# Revit family: equip-sink-elkay-scrub-wall-esswc
name_source: partatom
category: Plumbing Fixtures
units: mm (PartAtom-declared; Revit-internal decimal feet)

## family parameters
Cut with Voids When Loaded = No
Host = Face
Part Type = Normal
Room Calculation Point = No
Round Connector Dimension = Use Radius
Shared = No

## types (3) — shared parameters
AC Power = No
Assembly Code = D2010410
Backsplash Height = 1' - 0"
Backsplash Width = 0' - 2"
Backsplash Width Hidden = 0' - 2"
Bowl Depth = 1' - 0"
Bubbler CW Flow Rate = 2 GPM
Bubbler Material = Metal - Steel - Stainless - Chrome
Bubbler Nominal Dia = 0' - 0 1/2"
Bubbler Nominal Radius = 0' - 0 1/4"
CW Flow Rate = 2 GPM
Cost = 1 $
Default Elevation = 2' - 4 9/32"
Description = Wash-Up Lavatory Sinks
Distance Between Rough-In Water Supplies = 0' - 8"
Drain Material = Metal - Steel - Stainless - Chrome
Drain Part = LK173
Faucet CL from Top Backsplash = 0' - 3"
Faucet Hole Dia = 0' - 1 1/2"
Faucet Hole One = No
Faucet Hole One Top = 0' - 0 1/8"
Faucet Hole One to CL = 0' - 4"
Faucet Hole Two = No
Faucet Hole Two Top = 0' - 0 1/8"
Faucet Material = Metal - Steel - Stainless - Chrome
Faucet Part = LK940-BP07-L2
Faucet Water Supply Radius = 0' - 0 3/16"
HW Flow Rate = 2 GPM
Hole One to Two = 0' - 8"
Hole Radius = 0' - 0 3/4"
Keynote = D2010410
Manufacturer = Elkay Manufacturing
MasterFormat Number = 22.42.16.16
MasterFormat Title = Commercial Sinks
Mechanical Mix Valve = No
No Mix Valve = No
Nominal Dia = 0' - 0 1/2"
Nominal Radius = 0' - 0 1/4"
OmniClass Code = 23.45.05.14.14.27
OmniClass Title = Service Sinks
Plan View 2D = No
Reference Level to Back Plane = 0' - 0"
Rough-In Sanitary Installation Height = 0' - 11"
Rough-In Sanitary Right From CL Sink = 0' - 0"
Rough-In Water Supply Distance Left from CL Sink = 0' - 4"
Rough-In Water Supply Installation Height = 3' - 7 9/32"
Sanitary Flow Rate = 10 GPM
Sanitary Nominal Dia = 0' - 3"
Sanitary Nominal Radius = 0' - 1 1/2"
Sink Material = Metal - Steel - Stainless - Chrome
Sink Rim Front Width = 0' - 1 1/2"
Sink Rim Front Width Hidden = 0' - 1 1/2"
Sink Rim Left Width = 0' - 1 1/2"
Sink Rim Left Width Hidden = 0' - 1 1/2"
Sink Rim Right Width = 0' - 1 1/2"
Sink Rim Right Width Hidden = 0' - 1 1/2"
Sink San Conn Extr Visibility = No
Specification Sheet URL = http://www.elkayusa.com
Stem Material = Metal - Steel
Supply Line Mix Length = 0' - 0 1/2"
Thermostatic Mix Valve = No
Threaded Hose = No
URL = www.elkayusa.com
Valve Material = Metal - Brass
Vent Connection = Yes
zero-valued in all types: CWFU, HWFU, WFU

## per-type parameters (varying)
| type | Bowl Drain Location FB | Bowl Length | Bowl Width | Drain CL Front-Back | Drain CL LR to Left Bowl Edge | ESSW2319C | Hidden Length | Hidden Width | Model | Sink Length | Sink Part | Sink Width |
| ESSW2118C | 0' - 8" | 1' - 6" | 1' - 4" | 0' - 8" | 0' - 9" | Yes | 1' - 9" | 1' - 7 1/2" | ESS2118C | 1' - 9" | ESS21182 | 1' - 7 1/2" |
| ESSW2319C | 0' - 7 1/2" | 1' - 8" | 1' - 3" | 0' - 7 1/2" | 0' - 10" | No | 1' - 11" | 1' - 6 1/2" | ESSW2319C | 1' - 11" | ESS23192 | 1' - 6 1/2" |
| ESSW2520C | 0' - 8" | 1' - 10" | 1' - 4" | 0' - 8" | 0' - 11" | Yes | 2' - 1" | 1' - 7 1/2" | ESSW2520C | 2' - 1" | ESS25202 | 1' - 7 1/2" |

## geometry (parser evidence)
native form markers: Sweep x13
no freeform markers — native parametric forms only
